# Revit family: Zumtobel CRAFT II
name_source: partatom
category: Lighting Fixtures
revit_build: Autodesk Revit 2016 (Build: 20150220_1215(x64)
units: mm (PartAtom-declared; Revit-internal decimal feet)

## family parameters
Cut with Voids When Loaded = No
Host = Face
Light Source = Yes
OmniClass Number = 23.80.70.11
OmniClass Title = Luminaries for Internal Lighting
Part Type = Normal
Room Calculation Point = No
Round Connector Dimension = Use Diameter
Shared = No

## types (3) — shared parameters
Assembly Code = D5020200
Body = ZG_Metal_White
Color Filter = 16777215
Cover = ZG_Lamp_Self_llumination
Description = TEC LED luminaire
Dimming Lamp Color Temperature Shift = <None>
Emit Shape Visible in Rendering = No
Emit from Rectangle Length = 394 mm
Height = 109 mm
Lamp = LED
Manufacturer = Zumtobel Lighting
Tilt Angle = -90.00°
Voltage = 230 V
Width = 414 mm  [stored 1.35827 ft]
zero-valued in all types: Default Elevation

## per-type parameters (varying)
| type | Apparent Load | Craft Body L | Craft Body M | Craft TEC | Emit from Rectangle Width | Length | Model | No TEC | Photometric Web File | Suspension Distance | Suspension Vis | URL |
| CR2PL M17k-840 PC WB LDO WH | 114 VA | No | Yes | No | 498 mm | 518 mm | 42187254 | Yes | 42187254_(STD_LEO).IES | 356 mm | Yes | www.zumtobel.com/42187254 |
| CR2PL L27k-840 PC WB EVG WH | 164 VA | Yes | No | No | 1005 mm  [stored 3.29724 ft] | 1025 mm | 42187210 | Yes | 42187210_(STD_LEO).IES | 646 mm  [stored 2.11942 ft] | Yes | www.zumtobel.com/42187210 |
| CR2PL M17k-840 PC WB LDO TEC WH | 113 VA | No | Yes | Yes | 498 mm | 518 mm | 42187577 | No | 42187577_(STD_LEO).IES | 356 mm | No | www.zumtobel.com/42187577 |

note: [stored X ft] marks values corroborated as IEEE doubles in the binary element streams (Revit-internal decimal feet)

## geometry (parser evidence)
native form markers: Sweep x9
no freeform markers — native parametric forms only
